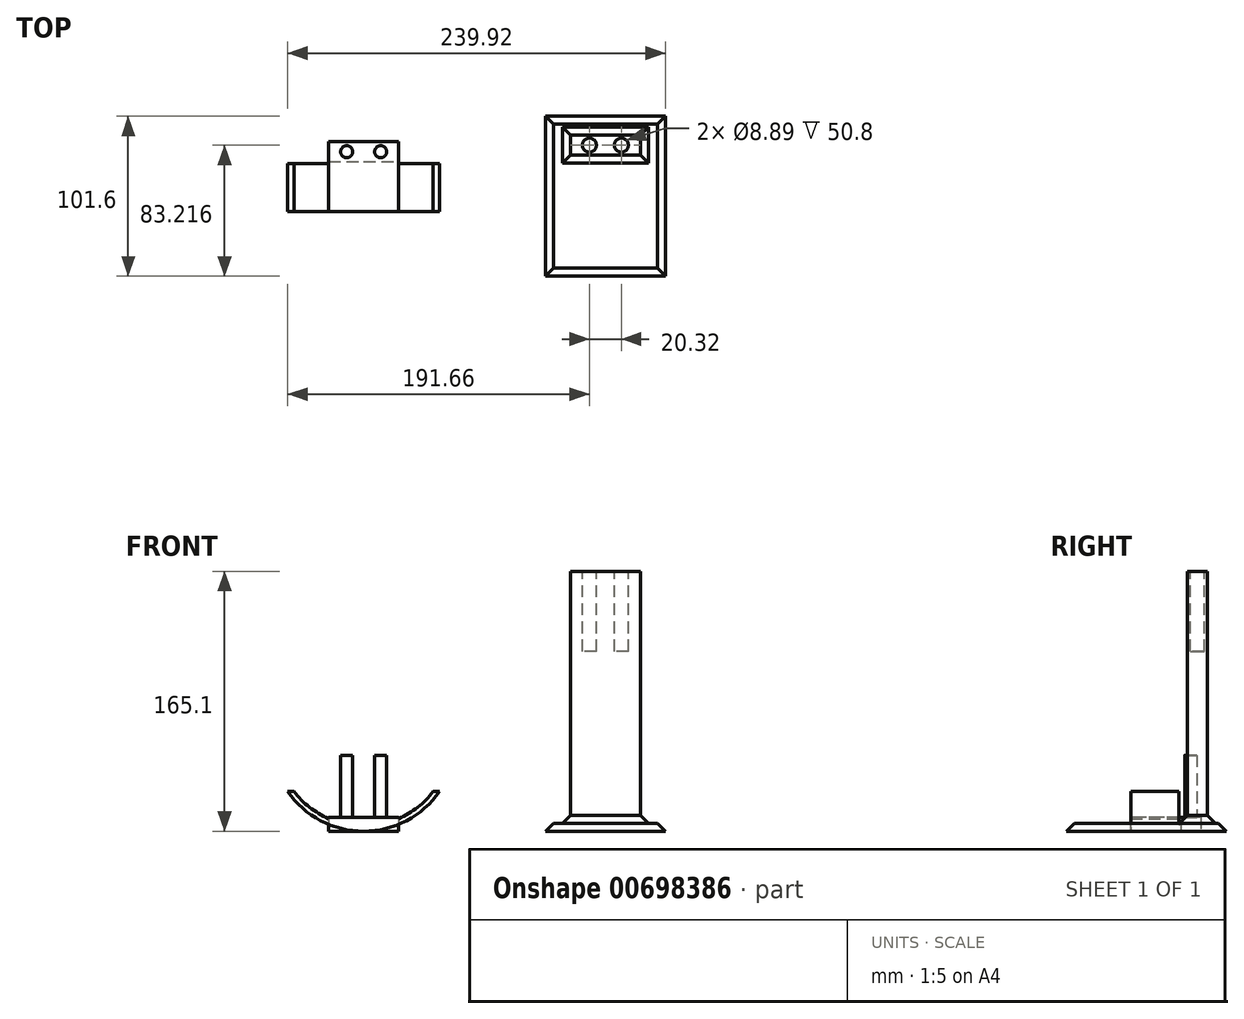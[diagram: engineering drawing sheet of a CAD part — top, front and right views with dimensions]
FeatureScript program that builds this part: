
annotation { "Feature Type Name" : "Feature", "Feature Type Description" : "" }
export const myFeature = defineFeature(function(context is Context, id is Id, definition is map)
    precondition{}
    {
        {
            var Q0;
            Q0=qCreatedBy(makeId("Top.planeOp"),FACE);
            var sketch = newSketch(context, id + "F0", { "sketchPlane" : qUnion([Q0])});
            skLineSegment(sketch, "E0.bottom", {"start": v(38.1, 50.8) * mm, "end": v(-38.1, 50.8) * mm});
            skLineSegment(sketch, "E0.top", {"start": v(38.1, -50.8) * mm, "end": v(-38.1, -50.8) * mm});
            skLineSegment(sketch, "E0.left", {"start": v(38.1, 50.8) * mm, "end": v(38.1, -50.8) * mm});
            skLineSegment(sketch, "E0.right", {"start": v(-38.1, 50.8) * mm, "end": v(-38.1, -50.8) * mm});
            skPoint(sketch, "E0.middle", {"position": v(0, 0) * mm});
            skLineSegment(sketch, "E1.bottom", {"start": v(22.23, 26.07) * mm, "end": v(-22.23, 26.07) * mm});
            skLineSegment(sketch, "E1.top", {"start": v(22.23, 38.77) * mm, "end": v(-22.23, 38.77) * mm});
            skLineSegment(sketch, "E1.left", {"start": v(22.23, 26.07) * mm, "end": v(22.23, 38.77) * mm});
            skLineSegment(sketch, "E1.right", {"start": v(-22.23, 26.07) * mm, "end": v(-22.23, 38.77) * mm});
            skPoint(sketch, "E1.middle", {"position": v(0, 32.42) * mm});
            skSolve(sketch);
        }
        {
            var Q0;
            Q0=makeQuery(id+"F0.imprint","IMPRINT",FACE,{"disambiguationData":[TD([[makeQuery(id+"F0.imprint","IMPRINT",EDGE,{"derivedFrom":sQuery(id+"F0.wireOp",EDGE,"E0.bottom")}),1.0]])]});
            extrude(context, id + "F1", {"entities" : qUnion([Q0]), "depth" : 5.08 * mm, "offsetDistance" : 25.4 * mm});
        }
        {
            var Q0;
            Q0=makeQuery(id+"F0.imprint","IMPRINT",FACE,{"disambiguationData":[TD([[makeQuery(id+"F0.imprint","IMPRINT",EDGE,{"derivedFrom":sQuery(id+"F0.wireOp",EDGE,"E1.bottom")}),-1.0]])]});
            extrude(context, id + "F2", {"entities" : qUnion([Q0]), "operationType" : NewBodyOperationType.ADD, "depth" : 165.1 * mm, "offsetDistance" : 25.4 * mm});
        }
        {
            var Q0;
            Q0=makeQuery(id+"F2.opExtrude","CAP_FACE",FACE,{"disambiguationData":[OSD([sQuery(id+"F0.wireOp",EDGE,"E1.bottom"),sQuery(id+"F0.wireOp",EDGE,"E1.top"),sQuery(id+"F0.wireOp",EDGE,"E1.left"),sQuery(id+"F0.wireOp",EDGE,"E1.right")])],"isStart":false});
            var sketch = newSketch(context, id + "F3", { "sketchPlane" : qUnion([Q0])});
            skCircle(sketch, "E2", {"center": v(-10.16, 32.42) * mm, "radius": 4.45 * mm});
            skPoint(sketch, "E2.centerSnap0", {"position": v(-22.23, 32.42) * mm});
            skCircle(sketch, "E3", {"center": v(10.16, 32.42) * mm, "radius": 4.45 * mm});
            skPoint(sketch, "E3.centerSnap0", {"position": v(22.23, 32.42) * mm});
            skSolve(sketch);
        }
        {
            var Q0;
            Q0=makeQuery(id+"F3.imprint","IMPRINT",FACE,{"disambiguationData":[TD([[makeQuery(id+"F3.imprint","IMPRINT",EDGE,{"derivedFrom":sQuery(id+"F3.wireOp",EDGE,"E2")}),1.0]])]});
            var Q1;
            Q1=makeQuery(id+"F3.imprint","IMPRINT",FACE,{"disambiguationData":[TD([[makeQuery(id+"F3.imprint","IMPRINT",EDGE,{"derivedFrom":sQuery(id+"F3.wireOp",EDGE,"E3")}),1.0]])]});
            extrude(context, id + "F4", {"entities" : qUnion([Q0, Q1]), "operationType" : NewBodyOperationType.REMOVE, "oppositeDirection" : true, "depth" : 50.8 * mm, "offsetDistance" : 25.4 * mm});
        }
        {
            var Q0;
            Q0=qCreatedBy(makeId("Top.planeOp"),FACE);
            var sketch = newSketch(context, id + "F5", { "sketchPlane" : qUnion([Q0])});
            skLineSegment(sketch, "E4.bottom", {"start": v(-175.78, 34.62) * mm, "end": v(-131.33, 34.62) * mm});
            skLineSegment(sketch, "E4.top", {"start": v(-175.78, 21.92) * mm, "end": v(-131.33, 21.92) * mm});
            skLineSegment(sketch, "E4.left", {"start": v(-175.78, 34.62) * mm, "end": v(-175.78, 21.92) * mm});
            skLineSegment(sketch, "E4.right", {"start": v(-131.33, 34.62) * mm, "end": v(-131.33, 21.92) * mm});
            skCircle(sketch, "E5", {"center": v(-164.35, 28.27) * mm, "radius": 3.81 * mm});
            skPoint(sketch, "E5.centerSnap0", {"position": v(-175.78, 28.27) * mm});
            skCircle(sketch, "E6", {"center": v(-142.76, 28.27) * mm, "radius": 3.81 * mm});
            skPoint(sketch, "E6.centerSnap0", {"position": v(-131.33, 28.27) * mm});
            skSolve(sketch);
        }
        {
            var Q0;
            Q0=makeQuery(id+"F5.imprint","IMPRINT",FACE,{"disambiguationData":[TD([[makeQuery(id+"F5.imprint","IMPRINT",EDGE,{"derivedFrom":sQuery(id+"F5.wireOp",EDGE,"E4.bottom")}),-1.0]])]});
            extrude(context, id + "F6", {"entities" : qUnion([Q0]), "depth" : 8.9 * mm, "offsetDistance" : 25.4 * mm});
        }
        {
            var Q0;
            Q0=makeQuery(id+"F5.imprint","IMPRINT",FACE,{"disambiguationData":[TD([[makeQuery(id+"F5.imprint","IMPRINT",EDGE,{"derivedFrom":sQuery(id+"F5.wireOp",EDGE,"E5")}),1.0]])]});
            var Q1;
            Q1=makeQuery(id+"F5.imprint","IMPRINT",FACE,{"disambiguationData":[TD([[makeQuery(id+"F5.imprint","IMPRINT",EDGE,{"derivedFrom":sQuery(id+"F5.wireOp",EDGE,"E6")}),1.0]])]});
            extrude(context, id + "F7", {"entities" : qUnion([Q0, Q1]), "operationType" : NewBodyOperationType.ADD, "depth" : 48.26 * mm, "offsetDistance" : 25.4 * mm});
        }
        {
            var Q0;
            Q0=makeQuery(id+"F6.opExtrude","SWEPT_FACE",FACE,{"disambiguationData":[OSD([sQuery(id+"F5.wireOp",EDGE,"E4.top")])]});
            var sketch = newSketch(context, id + "F8", { "sketchPlane" : qUnion([Q0])});
            skArc(sketch, "E7", {"start": v(-201.82, 25.4) * mm, "mid": v(-153.56, 0) * mm, "end": v(-105.3, 25.4) * mm});
            skPoint(sketch, "E7.centerSnap0", {"position": v(-153.56, 8.9) * mm});
            skLineSegment(sketch, "E8", {"start": v(-201.82, 25.4) * mm, "end": v(-105.3, 25.4) * mm});
            skArc(sketch, "E9.0", {"start": v(-207.45, 46.42) * mm, "mid": v(-153.56, 3.3) * mm, "end": v(-99.66, 46.42) * mm});
            skSolve(sketch);
        }
        {
            var Q0;
            {var subQ0=sQuery(id+"F8.wireOp",EDGE,"E7");var subQ1=sQuery(id+"F5.wireOp",EDGE,"E4.top");var subQ6=makeQuery(id+"F8.imprint","INTERSECT",VERTEX,{"derivedFrom":[makeQuery(id+"F6.opExtrude","CAP_EDGE",EDGE,{"disambiguationData":[OSD([subQ1])],"isStart":true}),subQ0]});Q0=makeQuery(id+"F8.imprint","IMPRINT",FACE,{"disambiguationData":[TD([[makeQuery(id+"F8.imprint","IMPRINT",EDGE,{"disambiguationData":[TD([[subQ6,1.0]])],"derivedFrom":subQ0}),1.0]])]});}
            var Q1;
            {var subQ0=sQuery(id+"F8.wireOp",EDGE,"E8");var subQ1=sQuery(id+"F8.wireOp",EDGE,"E7");var subQ2=makeQuery(id+"F8.imprint","INTERSECT",VERTEX,{"disambiguationData":[OD(1.0)],"derivedFrom":[subQ1,subQ0]});Q1=makeQuery(id+"F8.imprint","IMPRINT",FACE,{"disambiguationData":[TD([[makeQuery(id+"F8.imprint","IMPRINT",EDGE,{"disambiguationData":[TD([[subQ2,1.0]])],"derivedFrom":subQ0}),-1.0]])]});}
            var Q2;
            {var subQ0=sQuery(id+"F8.wireOp",EDGE,"E8");var subQ1=sQuery(id+"F8.wireOp",EDGE,"E7");var subQ2=makeQuery(id+"F8.imprint","INTERSECT",VERTEX,{"disambiguationData":[OD(0.0)],"derivedFrom":[subQ1,subQ0]});Q2=makeQuery(id+"F8.imprint","IMPRINT",FACE,{"disambiguationData":[TD([[makeQuery(id+"F8.imprint","IMPRINT",EDGE,{"disambiguationData":[TD([[subQ2,-1.0]])],"derivedFrom":subQ0}),-1.0]])]});}
            var Q3;
            {var subQ1=sQuery(id+"F5.wireOp",EDGE,"E4.top");var subQ6=makeQuery(id+"F6.opExtrude","CAP_EDGE",EDGE,{"disambiguationData":[OSD([subQ1])],"isStart":false});Q3=makeQuery(id+"F8.imprint","IMPRINT",FACE,{"disambiguationData":[TD([[makeQuery(id+"F8.imprint","IMPRINT",EDGE,{"derivedFrom":subQ6}),-1.0]])]});}
            extrude(context, id + "F9", {"entities" : qUnion([Q0, Q1, Q2, Q3]), "operationType" : NewBodyOperationType.ADD, "depth" : 31.75 * mm, "offsetDistance" : 25.4 * mm});
        }
        {
            var Q0;
            {var subQ0=sQuery(id+"F8.wireOp",EDGE,"E7");var subQ1=sQuery(id+"F5.wireOp",EDGE,"E4.right");var subQ3=sQuery(id+"F8.wireOp",EDGE,"E8");var subQ4=sQuery(id+"F8.wireOp",EDGE,"E9.0");Q0=makeQuery(id+"F9.boolean.opBoolean","SPLIT",FACE,{"disambiguationData":[TD([makeQuery(id+"F6.opExtrude","SWEPT_FACE",FACE,{"disambiguationData":[OSD([subQ1])]})])],"derivedFrom":makeQuery(id+"F9.opExtrude","CAP_FACE",FACE,{"disambiguationData":[OSD([subQ0,subQ3,subQ4])],"isStart":true})});}
            var Q1;
            {var subQ0=sQuery(id+"F8.wireOp",EDGE,"E7");var subQ1=sQuery(id+"F5.wireOp",EDGE,"E4.left");var subQ3=sQuery(id+"F8.wireOp",EDGE,"E8");var subQ4=sQuery(id+"F8.wireOp",EDGE,"E9.0");Q1=makeQuery(id+"F9.boolean.opBoolean","SPLIT",FACE,{"disambiguationData":[TD([makeQuery(id+"F6.opExtrude","SWEPT_FACE",FACE,{"disambiguationData":[OSD([subQ1])]})])],"derivedFrom":makeQuery(id+"F9.opExtrude","CAP_FACE",FACE,{"disambiguationData":[OSD([subQ0,subQ3,subQ4])],"isStart":true})});}
            extrude(context, id + "F10", {"entities" : qUnion([Q0, Q1]), "operationType" : NewBodyOperationType.REMOVE, "oppositeDirection" : true, "depth" : 1.27 * mm, "offsetDistance" : 25.4 * mm});
        }
        {
            var Q0;
            Q0=makeQuery(id+"F1.opExtrude","CAP_FACE",FACE,{"disambiguationData":[OSD([sQuery(id+"F0.wireOp",EDGE,"E0.bottom"),sQuery(id+"F0.wireOp",EDGE,"E0.top"),sQuery(id+"F0.wireOp",EDGE,"E0.left"),sQuery(id+"F0.wireOp",EDGE,"E0.right"),sQuery(id+"F0.wireOp",EDGE,"E1.bottom"),sQuery(id+"F0.wireOp",EDGE,"E1.top"),sQuery(id+"F0.wireOp",EDGE,"E1.left"),sQuery(id+"F0.wireOp",EDGE,"E1.right")])],"isStart":false});
            chamfer(context, id + "F11", {"entities" : qUnion([Q0]), "width" : 5.08 * mm, "tangentPropagation" : true});
        }
    });
